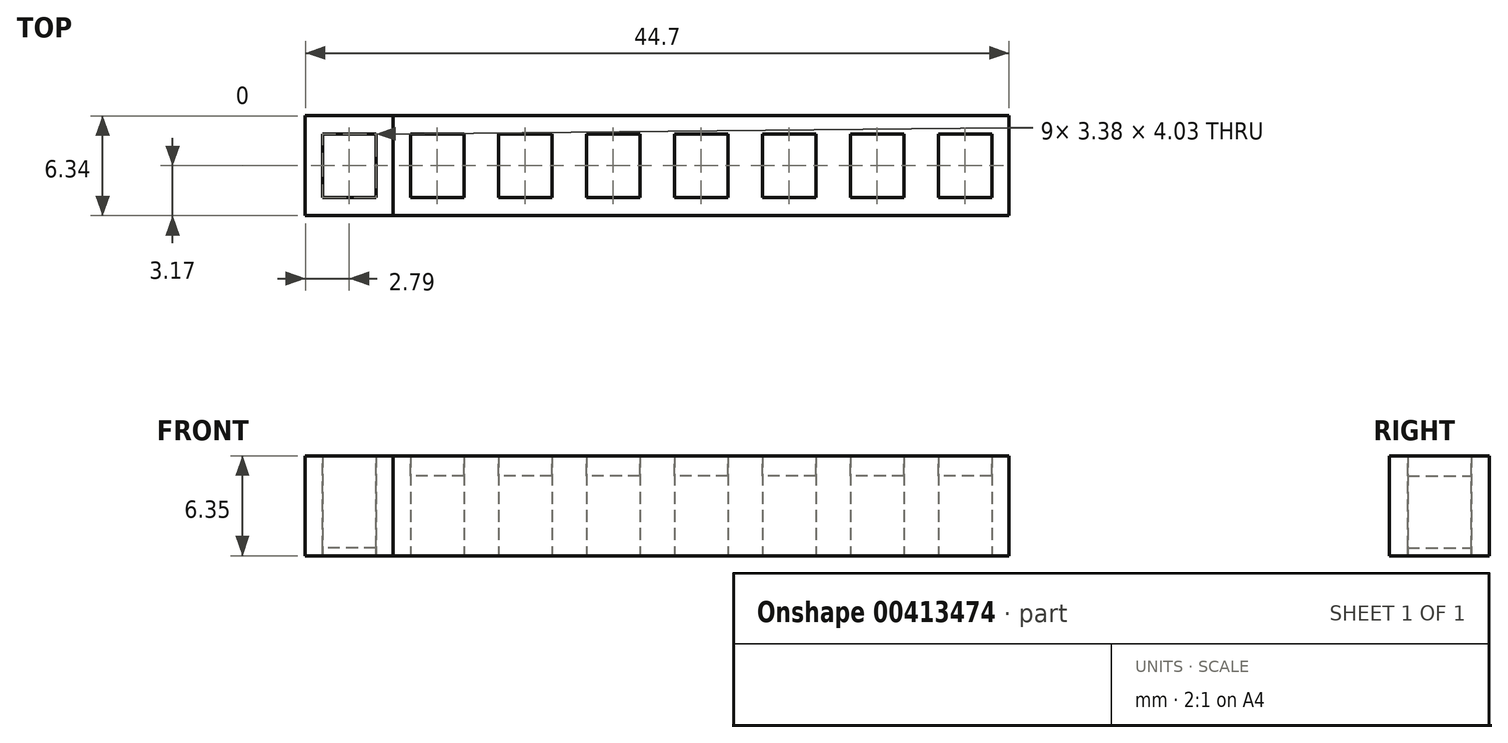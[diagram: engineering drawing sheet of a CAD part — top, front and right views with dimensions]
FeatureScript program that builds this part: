
annotation { "Feature Type Name" : "Feature", "Feature Type Description" : "" }
export const myFeature = defineFeature(function(context is Context, id is Id, definition is map)
    precondition{}
    {
        {
            var Q0;
            Q0=qCreatedBy(makeId("Top.planeOp"),FACE);
            var sketch = newSketch(context, id + "F0", { "sketchPlane" : qUnion([Q0])});
            skLineSegment(sketch, "E0.bottom", {"start": v(2.8, -3.17) * mm, "end": v(-2.8, -3.18) * mm});
            skLineSegment(sketch, "E0.top", {"start": v(2.8, 3.18) * mm, "end": v(-2.8, 3.18) * mm});
            skLineSegment(sketch, "E0.left", {"start": v(2.8, -3.17) * mm, "end": v(2.8, 3.18) * mm});
            skLineSegment(sketch, "E0.right", {"start": v(-2.8, -3.18) * mm, "end": v(-2.8, 3.18) * mm});
            skPoint(sketch, "E0.middle", {"position": v(0, 0) * mm});
            skLineSegment(sketch, "E1.bottom", {"start": v(1.7, -2.01) * mm, "end": v(-1.7, -2.01) * mm});
            skLineSegment(sketch, "E1.top", {"start": v(1.7, 2.01) * mm, "end": v(-1.7, 2.01) * mm});
            skLineSegment(sketch, "E1.left", {"start": v(1.7, -2.01) * mm, "end": v(1.7, 2.01) * mm});
            skLineSegment(sketch, "E1.right", {"start": v(-1.7, -2.01) * mm, "end": v(-1.7, 2.01) * mm});
            skLineSegment(sketch, "E2.bottom", {"start": v(8.38, -3.17) * mm, "end": v(2.8, -3.17) * mm});
            skLineSegment(sketch, "E2.top", {"start": v(8.38, 3.18) * mm, "end": v(2.8, 3.18) * mm});
            skLineSegment(sketch, "E2.left", {"start": v(8.38, -3.17) * mm, "end": v(8.38, 3.18) * mm});
            skPoint(sketch, "E2.middle", {"position": v(5.59, 0) * mm});
            skLineSegment(sketch, "E3.bottom", {"start": v(7.28, -2.01) * mm, "end": v(3.9, -2.01) * mm});
            skLineSegment(sketch, "E3.top", {"start": v(7.28, 2.01) * mm, "end": v(3.9, 2.01) * mm});
            skLineSegment(sketch, "E3.left", {"start": v(7.28, -2.01) * mm, "end": v(7.28, 2.01) * mm});
            skLineSegment(sketch, "E3.right", {"start": v(3.9, -2.01) * mm, "end": v(3.9, 2.01) * mm});
            skLineSegment(sketch, "E4.bottom", {"start": v(13.97, -3.17) * mm, "end": v(8.38, -3.17) * mm});
            skLineSegment(sketch, "E4.top", {"start": v(13.97, 3.18) * mm, "end": v(8.38, 3.18) * mm});
            skLineSegment(sketch, "E4.left", {"start": v(13.97, -3.17) * mm, "end": v(13.97, 3.18) * mm});
            skPoint(sketch, "E4.middle", {"position": v(11.18, 0) * mm});
            skLineSegment(sketch, "E5.bottom", {"start": v(12.87, -2.01) * mm, "end": v(9.48, -2.01) * mm});
            skLineSegment(sketch, "E5.top", {"start": v(12.87, 2.01) * mm, "end": v(9.48, 2.01) * mm});
            skLineSegment(sketch, "E5.left", {"start": v(12.87, -2.01) * mm, "end": v(12.87, 2.01) * mm});
            skLineSegment(sketch, "E5.right", {"start": v(9.48, -2.01) * mm, "end": v(9.48, 2.01) * mm});
            skLineSegment(sketch, "E6.bottom", {"start": v(19.56, -3.17) * mm, "end": v(13.97, -3.17) * mm});
            skLineSegment(sketch, "E6.top", {"start": v(19.56, 3.18) * mm, "end": v(13.97, 3.18) * mm});
            skLineSegment(sketch, "E6.left", {"start": v(19.56, -3.17) * mm, "end": v(19.56, 3.18) * mm});
            skPoint(sketch, "E6.middle", {"position": v(16.76, 0) * mm});
            skLineSegment(sketch, "E7.bottom", {"start": v(18.46, -2.01) * mm, "end": v(15.07, -2.01) * mm});
            skLineSegment(sketch, "E7.top", {"start": v(18.46, 2.01) * mm, "end": v(15.07, 2.01) * mm});
            skLineSegment(sketch, "E7.left", {"start": v(18.46, -2.01) * mm, "end": v(18.46, 2.01) * mm});
            skLineSegment(sketch, "E7.right", {"start": v(15.07, -2.01) * mm, "end": v(15.07, 2.01) * mm});
            skLineSegment(sketch, "E8.bottom", {"start": v(25.15, -3.17) * mm, "end": v(19.56, -3.17) * mm});
            skLineSegment(sketch, "E8.top", {"start": v(25.15, 3.18) * mm, "end": v(19.56, 3.18) * mm});
            skLineSegment(sketch, "E8.left", {"start": v(25.15, -3.17) * mm, "end": v(25.15, 3.18) * mm});
            skPoint(sketch, "E8.middle", {"position": v(22.35, 0) * mm});
            skLineSegment(sketch, "E9.bottom", {"start": v(24.04, -2.01) * mm, "end": v(20.66, -2.01) * mm});
            skLineSegment(sketch, "E9.top", {"start": v(24.04, 2.01) * mm, "end": v(20.66, 2.01) * mm});
            skLineSegment(sketch, "E9.left", {"start": v(24.04, -2.01) * mm, "end": v(24.04, 2.01) * mm});
            skLineSegment(sketch, "E9.right", {"start": v(20.66, -2.01) * mm, "end": v(20.66, 2.01) * mm});
            skLineSegment(sketch, "E10.bottom", {"start": v(30.73, -3.17) * mm, "end": v(25.15, -3.17) * mm});
            skLineSegment(sketch, "E10.top", {"start": v(30.73, 3.18) * mm, "end": v(25.15, 3.18) * mm});
            skLineSegment(sketch, "E10.left", {"start": v(30.73, -3.17) * mm, "end": v(30.73, 3.18) * mm});
            skPoint(sketch, "E10.middle", {"position": v(27.94, 0) * mm});
            skLineSegment(sketch, "E11.bottom", {"start": v(29.63, -2.01) * mm, "end": v(26.25, -2.01) * mm});
            skLineSegment(sketch, "E11.top", {"start": v(29.63, 2.01) * mm, "end": v(26.25, 2.01) * mm});
            skLineSegment(sketch, "E11.left", {"start": v(29.63, -2.01) * mm, "end": v(29.63, 2.01) * mm});
            skLineSegment(sketch, "E11.right", {"start": v(26.25, -2.01) * mm, "end": v(26.25, 2.01) * mm});
            skLineSegment(sketch, "E12.bottom", {"start": v(36.32, -3.17) * mm, "end": v(30.73, -3.17) * mm});
            skLineSegment(sketch, "E12.top", {"start": v(36.32, 3.18) * mm, "end": v(30.73, 3.18) * mm});
            skLineSegment(sketch, "E12.left", {"start": v(36.32, -3.17) * mm, "end": v(36.32, 3.18) * mm});
            skPoint(sketch, "E12.middle", {"position": v(33.53, 0) * mm});
            skLineSegment(sketch, "E13.bottom", {"start": v(35.22, -2.01) * mm, "end": v(31.84, -2.01) * mm});
            skLineSegment(sketch, "E13.top", {"start": v(35.22, 2.01) * mm, "end": v(31.84, 2.01) * mm});
            skLineSegment(sketch, "E13.left", {"start": v(35.22, -2.01) * mm, "end": v(35.22, 2.01) * mm});
            skLineSegment(sketch, "E13.right", {"start": v(31.84, -2.01) * mm, "end": v(31.84, 2.01) * mm});
            skLineSegment(sketch, "E14.bottom", {"start": v(41.91, -3.17) * mm, "end": v(36.32, -3.17) * mm});
            skLineSegment(sketch, "E14.top", {"start": v(41.91, 3.18) * mm, "end": v(36.32, 3.18) * mm});
            skLineSegment(sketch, "E14.left", {"start": v(41.91, -3.17) * mm, "end": v(41.91, 3.18) * mm});
            skPoint(sketch, "E14.middle", {"position": v(39.12, 0) * mm});
            skLineSegment(sketch, "E15.bottom", {"start": v(40.8, -2.01) * mm, "end": v(37.42, -2.01) * mm});
            skLineSegment(sketch, "E15.top", {"start": v(40.8, 2.01) * mm, "end": v(37.42, 2.01) * mm});
            skLineSegment(sketch, "E15.left", {"start": v(40.8, -2.01) * mm, "end": v(40.8, 2.01) * mm});
            skLineSegment(sketch, "E15.right", {"start": v(37.42, -2.01) * mm, "end": v(37.42, 2.01) * mm});
            skSolve(sketch);
        }
        {
            var Q0;
            Q0=makeQuery(id+"F0.imprint","IMPRINT",FACE,{"disambiguationData":[TD([[makeQuery(id+"F0.imprint","IMPRINT",EDGE,{"derivedFrom":sQuery(id+"F0.wireOp",EDGE,"E0.bottom")}),-1.0]])]});
            extrude(context, id + "F1", {"entities" : qUnion([Q0]), "depth" : 6.35 * mm});
        }
        {
            var Q0;
            Q0=makeQuery(id+"F1.opExtrude","CAP_FACE",FACE,{"disambiguationData":[OSD([sQuery(id+"F0.wireOp",EDGE,"E0.bottom"),sQuery(id+"F0.wireOp",EDGE,"E0.top"),sQuery(id+"F0.wireOp",EDGE,"E0.left"),sQuery(id+"F0.wireOp",EDGE,"E0.right"),sQuery(id+"F0.wireOp",EDGE,"E1.bottom"),sQuery(id+"F0.wireOp",EDGE,"E1.top"),sQuery(id+"F0.wireOp",EDGE,"E1.left"),sQuery(id+"F0.wireOp",EDGE,"E1.right")])],"isStart":false});
            var sketch = newSketch(context, id + "F2", { "sketchPlane" : qUnion([Q0])});
            skLineSegment(sketch, "E16.bottom", {"start": v(1.7, -2.01) * mm, "end": v(-1.7, -2.01) * mm});
            skLineSegment(sketch, "E16.top", {"start": v(1.7, 2.01) * mm, "end": v(-1.7, 2.01) * mm});
            skLineSegment(sketch, "E16.left", {"start": v(1.7, -2.01) * mm, "end": v(1.7, 2.01) * mm});
            skLineSegment(sketch, "E16.right", {"start": v(-1.7, -2.01) * mm, "end": v(-1.7, 2.01) * mm});
            skPoint(sketch, "E16.middle", {"position": v(0, 0) * mm});
            skSolve(sketch);
        }
        {
            var Q0;
            Q0=makeQuery(id+"F2.imprint","IMPRINT",FACE,{"disambiguationData":[TD([[makeQuery(id+"F2.imprint","IMPRINT",EDGE,{"derivedFrom":sQuery(id+"F2.wireOp",EDGE,"E16.bottom")}),-1.0]])]});
            extrude(context, id + "F3", {"entities" : qUnion([Q0]), "oppositeDirection" : true, "depth" : 5.84 * mm});
        }
        {
            var Q0;
            Q0=makeQuery(id+"F3.opExtrude","CAP_FACE",FACE,{"disambiguationData":[OSD([sQuery(id+"F2.wireOp",EDGE,"E16.bottom"),sQuery(id+"F2.wireOp",EDGE,"E16.top"),sQuery(id+"F2.wireOp",EDGE,"E16.left"),sQuery(id+"F2.wireOp",EDGE,"E16.right")])],"isStart":false});
            extrude(context, id + "F4", {"entities" : qUnion([Q0]), "depth" : 0.5 * mm});
        }
        {
            var Q0;
            Q0 = qSketchRegion(id + "F0", true);
            extrude(context, id + "F5", {"entities" : qUnion([Q0]), "depth" : 6.35 * mm});
        }
        {
            var Q0;
            Q0=makeQuery(id+"F5.opExtrude","CAP_FACE",FACE,{"disambiguationData":[OSD([sQuery(id+"F0.wireOp",EDGE,"E0.bottom"),sQuery(id+"F0.wireOp",EDGE,"E0.top"),sQuery(id+"F0.wireOp",EDGE,"E0.right"),sQuery(id+"F0.wireOp",EDGE,"E1.bottom"),sQuery(id+"F0.wireOp",EDGE,"E1.top"),sQuery(id+"F0.wireOp",EDGE,"E1.left"),sQuery(id+"F0.wireOp",EDGE,"E1.right"),sQuery(id+"F0.wireOp",EDGE,"E2.bottom"),sQuery(id+"F0.wireOp",EDGE,"E2.top"),sQuery(id+"F0.wireOp",EDGE,"E3.bottom"),sQuery(id+"F0.wireOp",EDGE,"E3.top"),sQuery(id+"F0.wireOp",EDGE,"E3.left"),sQuery(id+"F0.wireOp",EDGE,"E3.right"),sQuery(id+"F0.wireOp",EDGE,"E4.bottom"),sQuery(id+"F0.wireOp",EDGE,"E4.top"),sQuery(id+"F0.wireOp",EDGE,"E5.bottom"),sQuery(id+"F0.wireOp",EDGE,"E5.top"),sQuery(id+"F0.wireOp",EDGE,"E5.left"),sQuery(id+"F0.wireOp",EDGE,"E5.right"),sQuery(id+"F0.wireOp",EDGE,"E6.bottom"),sQuery(id+"F0.wireOp",EDGE,"E6.top"),sQuery(id+"F0.wireOp",EDGE,"E7.bottom"),sQuery(id+"F0.wireOp",EDGE,"E7.top"),sQuery(id+"F0.wireOp",EDGE,"E7.left"),sQuery(id+"F0.wireOp",EDGE,"E7.right"),sQuery(id+"F0.wireOp",EDGE,"E8.bottom"),sQuery(id+"F0.wireOp",EDGE,"E8.top"),sQuery(id+"F0.wireOp",EDGE,"E9.bottom"),sQuery(id+"F0.wireOp",EDGE,"E9.top"),sQuery(id+"F0.wireOp",EDGE,"E9.left"),sQuery(id+"F0.wireOp",EDGE,"E9.right"),sQuery(id+"F0.wireOp",EDGE,"E10.bottom"),sQuery(id+"F0.wireOp",EDGE,"E10.top"),sQuery(id+"F0.wireOp",EDGE,"E11.bottom"),sQuery(id+"F0.wireOp",EDGE,"E11.top"),sQuery(id+"F0.wireOp",EDGE,"E11.left"),sQuery(id+"F0.wireOp",EDGE,"E11.right"),sQuery(id+"F0.wireOp",EDGE,"E12.bottom"),sQuery(id+"F0.wireOp",EDGE,"E12.top"),sQuery(id+"F0.wireOp",EDGE,"E13.bottom"),sQuery(id+"F0.wireOp",EDGE,"E13.top"),sQuery(id+"F0.wireOp",EDGE,"E13.left"),sQuery(id+"F0.wireOp",EDGE,"E13.right"),sQuery(id+"F0.wireOp",EDGE,"E14.bottom"),sQuery(id+"F0.wireOp",EDGE,"E14.top"),sQuery(id+"F0.wireOp",EDGE,"E14.left"),sQuery(id+"F0.wireOp",EDGE,"E15.bottom"),sQuery(id+"F0.wireOp",EDGE,"E15.top"),sQuery(id+"F0.wireOp",EDGE,"E15.left"),sQuery(id+"F0.wireOp",EDGE,"E15.right")])],"isStart":false});
            var sketch = newSketch(context, id + "F6", { "sketchPlane" : qUnion([Q0])});
            skLineSegment(sketch, "E17.bottom", {"start": v(3.9, 2.01) * mm, "end": v(7.28, 2.01) * mm});
            skLineSegment(sketch, "E17.top", {"start": v(3.9, -2.01) * mm, "end": v(7.28, -2.01) * mm});
            skLineSegment(sketch, "E17.left", {"start": v(3.9, 2.01) * mm, "end": v(3.9, -2.01) * mm});
            skLineSegment(sketch, "E17.right", {"start": v(7.28, 2.01) * mm, "end": v(7.28, -2.01) * mm});
            skLineSegment(sketch, "E18.bottom", {"start": v(9.48, 2.01) * mm, "end": v(12.87, 2.01) * mm});
            skLineSegment(sketch, "E18.top", {"start": v(9.48, -2.01) * mm, "end": v(12.87, -2.01) * mm});
            skLineSegment(sketch, "E18.left", {"start": v(9.48, 2.01) * mm, "end": v(9.48, -2.01) * mm});
            skLineSegment(sketch, "E18.right", {"start": v(12.87, 2.01) * mm, "end": v(12.87, -2.01) * mm});
            skLineSegment(sketch, "E19.bottom", {"start": v(15.07, 2.01) * mm, "end": v(18.46, 2.01) * mm});
            skLineSegment(sketch, "E19.top", {"start": v(15.07, -2.01) * mm, "end": v(18.46, -2.01) * mm});
            skLineSegment(sketch, "E19.left", {"start": v(15.07, 2.01) * mm, "end": v(15.07, -2.01) * mm});
            skLineSegment(sketch, "E19.right", {"start": v(18.46, 2.01) * mm, "end": v(18.46, -2.01) * mm});
            skLineSegment(sketch, "E20.bottom", {"start": v(20.66, 2.01) * mm, "end": v(24.04, 2.01) * mm});
            skLineSegment(sketch, "E20.top", {"start": v(20.66, -2.01) * mm, "end": v(24.04, -2.01) * mm});
            skLineSegment(sketch, "E20.left", {"start": v(20.66, 2.01) * mm, "end": v(20.66, -2.01) * mm});
            skLineSegment(sketch, "E20.right", {"start": v(24.04, 2.01) * mm, "end": v(24.04, -2.01) * mm});
            skLineSegment(sketch, "E21.bottom", {"start": v(26.25, 2.01) * mm, "end": v(29.63, 2.01) * mm});
            skLineSegment(sketch, "E21.top", {"start": v(26.25, -2.01) * mm, "end": v(29.63, -2.01) * mm});
            skLineSegment(sketch, "E21.left", {"start": v(26.25, 2.01) * mm, "end": v(26.25, -2.01) * mm});
            skLineSegment(sketch, "E21.right", {"start": v(29.63, 2.01) * mm, "end": v(29.63, -2.01) * mm});
            skLineSegment(sketch, "E22.bottom", {"start": v(31.84, 2.01) * mm, "end": v(35.22, 2.01) * mm});
            skLineSegment(sketch, "E22.top", {"start": v(31.84, -2.01) * mm, "end": v(35.22, -2.01) * mm});
            skLineSegment(sketch, "E22.left", {"start": v(31.84, 2.01) * mm, "end": v(31.84, -2.01) * mm});
            skLineSegment(sketch, "E22.right", {"start": v(35.22, 2.01) * mm, "end": v(35.22, -2.01) * mm});
            skLineSegment(sketch, "E23.bottom", {"start": v(37.42, 2.01) * mm, "end": v(40.8, 2.01) * mm});
            skLineSegment(sketch, "E23.top", {"start": v(37.42, -2.01) * mm, "end": v(40.8, -2.01) * mm});
            skLineSegment(sketch, "E23.left", {"start": v(37.42, 2.01) * mm, "end": v(37.42, -2.01) * mm});
            skLineSegment(sketch, "E23.right", {"start": v(40.8, 2.01) * mm, "end": v(40.8, -2.01) * mm});
            skSolve(sketch);
        }
        {
            var Q0;
            Q0=makeQuery(id+"F6.imprint","IMPRINT",FACE,{"disambiguationData":[TD([[makeQuery(id+"F6.imprint","IMPRINT",EDGE,{"derivedFrom":sQuery(id+"F6.wireOp",EDGE,"E17.bottom")}),1.0]])]});
            var Q1;
            Q1=makeQuery(id+"F6.imprint","IMPRINT",FACE,{"disambiguationData":[TD([[makeQuery(id+"F6.imprint","IMPRINT",EDGE,{"derivedFrom":sQuery(id+"F6.wireOp",EDGE,"E18.bottom")}),1.0]])]});
            var Q2;
            Q2=makeQuery(id+"F6.imprint","IMPRINT",FACE,{"disambiguationData":[TD([[makeQuery(id+"F6.imprint","IMPRINT",EDGE,{"derivedFrom":sQuery(id+"F6.wireOp",EDGE,"E19.bottom")}),1.0]])]});
            var Q3;
            Q3=makeQuery(id+"F6.imprint","IMPRINT",FACE,{"disambiguationData":[TD([[makeQuery(id+"F6.imprint","IMPRINT",EDGE,{"derivedFrom":sQuery(id+"F6.wireOp",EDGE,"E20.bottom")}),1.0]])]});
            var Q4;
            Q4=makeQuery(id+"F6.imprint","IMPRINT",FACE,{"disambiguationData":[TD([[makeQuery(id+"F6.imprint","IMPRINT",EDGE,{"derivedFrom":sQuery(id+"F6.wireOp",EDGE,"E21.bottom")}),1.0]])]});
            var Q5;
            Q5=makeQuery(id+"F6.imprint","IMPRINT",FACE,{"disambiguationData":[TD([[makeQuery(id+"F6.imprint","IMPRINT",EDGE,{"derivedFrom":sQuery(id+"F6.wireOp",EDGE,"E22.bottom")}),1.0]])]});
            var Q6;
            Q6=makeQuery(id+"F6.imprint","IMPRINT",FACE,{"disambiguationData":[TD([[makeQuery(id+"F6.imprint","IMPRINT",EDGE,{"derivedFrom":sQuery(id+"F6.wireOp",EDGE,"E23.bottom")}),1.0]])]});
            extrude(context, id + "F7", {"entities" : qUnion([Q0, Q1, Q2, Q3, Q4, Q5, Q6]), "oppositeDirection" : true, "depth" : 1.27 * mm});
        }
    });
